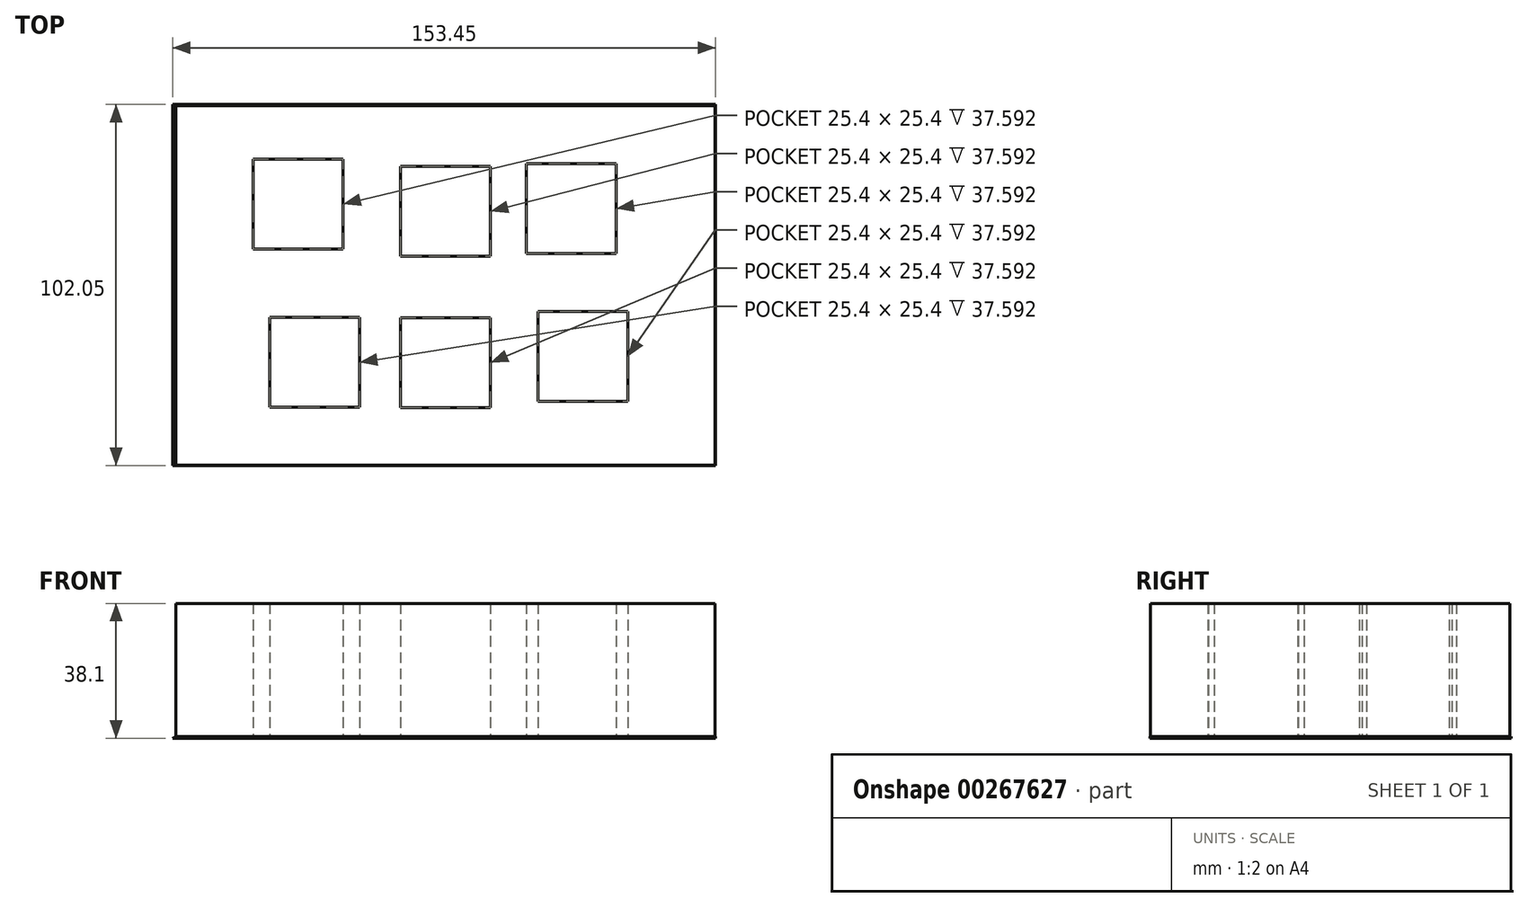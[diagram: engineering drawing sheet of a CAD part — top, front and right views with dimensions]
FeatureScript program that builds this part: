
annotation { "Feature Type Name" : "Feature", "Feature Type Description" : "" }
export const myFeature = defineFeature(function(context is Context, id is Id, definition is map)
    precondition{}
    {
        {
            var Q0;
            Q0=qCreatedBy(makeId("Top.planeOp"),FACE);
            var sketch = newSketch(context, id + "F0", { "sketchPlane" : qUnion([Q0])});
            skLineSegment(sketch, "E0.bottom", {"start": v(76.2, 50.8) * mm, "end": v(-76.2, 50.8) * mm});
            skLineSegment(sketch, "E0.top", {"start": v(76.2, -50.8) * mm, "end": v(-76.2, -50.8) * mm});
            skLineSegment(sketch, "E0.left", {"start": v(76.2, 50.8) * mm, "end": v(76.2, -50.8) * mm});
            skLineSegment(sketch, "E0.right", {"start": v(-76.2, 50.8) * mm, "end": v(-76.2, -50.8) * mm});
            skPoint(sketch, "E0.middle", {"position": v(0, 0) * mm});
            skSolve(sketch);
        }
        {
            var Q0;
            Q0=makeQuery(id+"F0.imprint","IMPRINT",FACE,{"disambiguationData":[TD([[makeQuery(id+"F0.imprint","IMPRINT",EDGE,{"derivedFrom":sQuery(id+"F0.wireOp",EDGE,"E0.bottom")}),1.0]])]});
            var sketch = newSketch(context, id + "F1", { "sketchPlane" : qUnion([Q0])});
            skLineSegment(sketch, "E1.bottom", {"start": v(-28.94, 10.34) * mm, "end": v(-54.34, 10.34) * mm});
            skLineSegment(sketch, "E1.top", {"start": v(-28.94, 35.74) * mm, "end": v(-54.34, 35.74) * mm});
            skLineSegment(sketch, "E1.left", {"start": v(-28.94, 10.34) * mm, "end": v(-28.94, 35.74) * mm});
            skLineSegment(sketch, "E1.right", {"start": v(-54.34, 10.34) * mm, "end": v(-54.34, 35.74) * mm});
            skPoint(sketch, "E1.middle", {"position": v(-41.64, 23.04) * mm});
            skLineSegment(sketch, "E2.bottom", {"start": v(12.7, 8.27) * mm, "end": v(-12.7, 8.27) * mm});
            skLineSegment(sketch, "E2.top", {"start": v(12.7, 33.67) * mm, "end": v(-12.7, 33.67) * mm});
            skLineSegment(sketch, "E2.left", {"start": v(12.7, 8.27) * mm, "end": v(12.7, 33.67) * mm});
            skLineSegment(sketch, "E2.right", {"start": v(-12.7, 8.27) * mm, "end": v(-12.7, 33.67) * mm});
            skPoint(sketch, "E2.middle", {"position": v(0, 20.97) * mm});
            skLineSegment(sketch, "E3.bottom", {"start": v(48.29, 9) * mm, "end": v(22.89, 9) * mm});
            skLineSegment(sketch, "E3.top", {"start": v(48.29, 34.4) * mm, "end": v(22.89, 34.4) * mm});
            skLineSegment(sketch, "E3.left", {"start": v(48.29, 9) * mm, "end": v(48.29, 34.4) * mm});
            skLineSegment(sketch, "E3.right", {"start": v(22.89, 9) * mm, "end": v(22.89, 34.4) * mm});
            skPoint(sketch, "E3.middle", {"position": v(35.59, 21.7) * mm});
            skLineSegment(sketch, "E4.bottom", {"start": v(51.54, -32.78) * mm, "end": v(26.14, -32.78) * mm});
            skLineSegment(sketch, "E4.top", {"start": v(51.54, -7.38) * mm, "end": v(26.14, -7.38) * mm});
            skLineSegment(sketch, "E4.left", {"start": v(51.54, -32.78) * mm, "end": v(51.54, -7.38) * mm});
            skLineSegment(sketch, "E4.right", {"start": v(26.14, -32.78) * mm, "end": v(26.14, -7.38) * mm});
            skPoint(sketch, "E4.middle", {"position": v(38.84, -20.08) * mm});
            skLineSegment(sketch, "E5.bottom", {"start": v(12.7, -34.56) * mm, "end": v(-12.7, -34.56) * mm});
            skLineSegment(sketch, "E5.top", {"start": v(12.7, -9.16) * mm, "end": v(-12.7, -9.16) * mm});
            skLineSegment(sketch, "E5.left", {"start": v(12.7, -34.56) * mm, "end": v(12.7, -9.16) * mm});
            skLineSegment(sketch, "E5.right", {"start": v(-12.7, -34.56) * mm, "end": v(-12.7, -9.16) * mm});
            skPoint(sketch, "E5.middle", {"position": v(0, -21.86) * mm});
            skLineSegment(sketch, "E6.bottom", {"start": v(-24.22, -34.4) * mm, "end": v(-49.62, -34.4) * mm});
            skLineSegment(sketch, "E6.top", {"start": v(-24.22, -9) * mm, "end": v(-49.62, -9) * mm});
            skLineSegment(sketch, "E6.left", {"start": v(-24.22, -34.4) * mm, "end": v(-24.22, -9) * mm});
            skLineSegment(sketch, "E6.right", {"start": v(-49.62, -34.4) * mm, "end": v(-49.62, -9) * mm});
            skPoint(sketch, "E6.middle", {"position": v(-36.92, -21.7) * mm});
            skSolve(sketch);
        }
        {
            var Q0;
            Q0=makeQuery(id+"F1.imprint","IMPRINT",FACE,{"disambiguationData":[TD([[makeQuery(id+"F1.imprint","IMPRINT",EDGE,{"derivedFrom":sQuery(id+"F1.wireOp",EDGE,"E1.bottom")}),1.0]])]});
            extrude(context, id + "F2", {"entities" : qUnion([Q0]), "depth" : 38.1 * mm});
        }
        {
            var Q0;
            Q0=makeQuery(id+"F0.imprint","IMPRINT",FACE,{"disambiguationData":[TD([[makeQuery(id+"F0.imprint","IMPRINT",EDGE,{"derivedFrom":sQuery(id+"F0.wireOp",EDGE,"E0.bottom")}),1.0]])]});
            var sketch = newSketch(context, id + "F3", { "sketchPlane" : qUnion([Q0])});
            skLineSegment(sketch, "E7.bottom", {"start": v(-77.1, -50.86) * mm, "end": v(76.36, -50.86) * mm});
            skLineSegment(sketch, "E7.top", {"start": v(-77.1, 51.2) * mm, "end": v(76.36, 51.2) * mm});
            skLineSegment(sketch, "E7.left", {"start": v(-77.1, -50.86) * mm, "end": v(-77.1, 51.2) * mm});
            skLineSegment(sketch, "E7.right", {"start": v(76.36, -50.86) * mm, "end": v(76.36, 51.2) * mm});
            skSolve(sketch);
        }
        {
            var Q0;
            Q0=makeQuery(id+"F3.imprint","IMPRINT",FACE,{"disambiguationData":[TD([[makeQuery(id+"F3.imprint","IMPRINT",EDGE,{"derivedFrom":sQuery(id+"F3.wireOp",EDGE,"E7.bottom")}),1.0]])]});
            extrude(context, id + "F4", {"entities" : qUnion([Q0]), "operationType" : NewBodyOperationType.ADD, "depth" : 0.5 * mm});
        }
        {
            var Q0;
            Q0=makeQuery(id+"F0.imprint","IMPRINT",FACE,{"disambiguationData":[TD([[makeQuery(id+"F0.imprint","IMPRINT",EDGE,{"derivedFrom":sQuery(id+"F0.wireOp",EDGE,"E0.bottom")}),1.0]])]});
            extrude(context, id + "F5", {"entities" : qUnion([Q0]), "operationType" : NewBodyOperationType.ADD, "depth" : 0.5 * mm});
        }
        {
            var Q0;
            Q0=makeQuery(id+"F4.opExtrude","CAP_EDGE",EDGE,{"disambiguationData":[OSD([sQuery(id+"F3.wireOp",EDGE,"E7.left")])],"isStart":false});
            fillet(context, id + "F6", {"entities" : qUnion([Q0]), "radius" : 5.08 * mm, "tangentPropagation" : true, "allowEdgeOverflow" : false});
        }
    });
